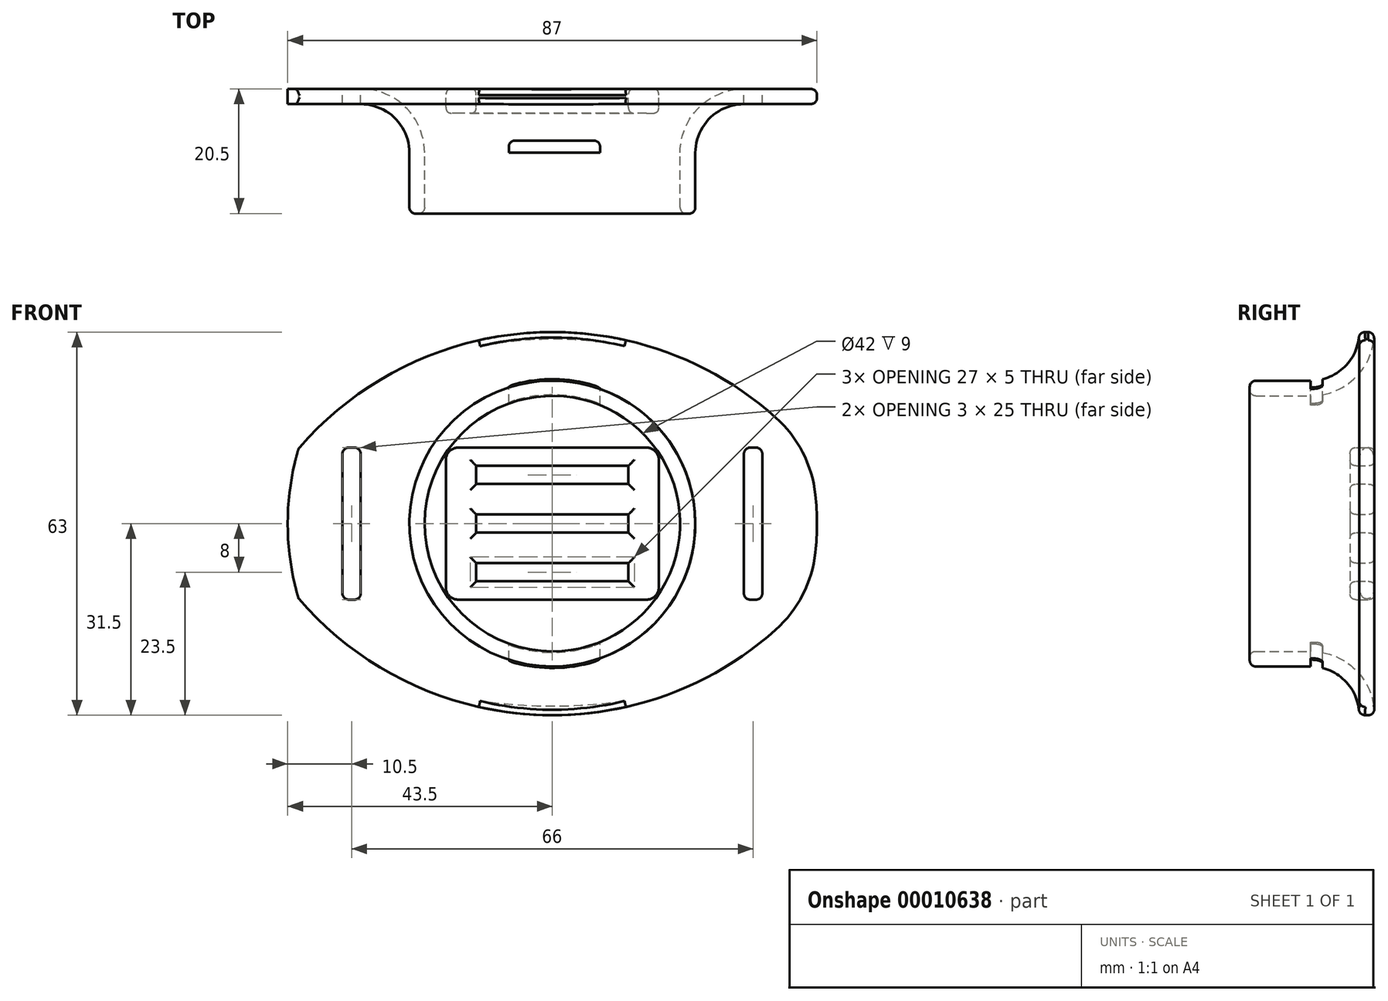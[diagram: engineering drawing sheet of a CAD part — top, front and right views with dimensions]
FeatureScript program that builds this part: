
annotation { "Feature Type Name" : "Feature", "Feature Type Description" : "" }
export const myFeature = defineFeature(function(context is Context, id is Id, definition is map)
    precondition{}
    {
        {
            var Q0;
            Q0=qCreatedBy(makeId("Front.planeOp"),FACE);
            var sketch = newSketch(context, id + "F0", { "sketchPlane" : qUnion([Q0])});
            skEllipse(sketch, "E0", {"center": v(0, 0) * mm, "majorRadius": 23.5 * mm, "minorRadius": 23.5 * mm, "majorAxis": v(1, 0)});
            skLineSegment(sketch, "E1", {"start": v(-23.5, 0) * mm, "end": v(23.5, 0) * mm, "construction": true});
            skLineSegment(sketch, "E2", {"start": v(0, -23.5) * mm, "end": v(0, 23.5) * mm, "construction": true});
            skCircle(sketch, "E3", {"center": v(0, 0) * mm, "radius": 21 * mm});
            skSolve(sketch);
        }
        {
            var Q0;
            Q0=makeQuery(id+"F0.imprint","IMPRINT",FACE,{"disambiguationData":[TD([[makeQuery(id+"F0.imprint","IMPRINT",EDGE,{"derivedFrom":sQuery(id+"F0.wireOp",EDGE,"E0")}),1.0]])]});
            extrude(context, id + "F1", {"entities" : qUnion([Q0]), "depth" : 10 * mm});
        }
        {
            var Q0;
            Q0=qCreatedBy(makeId("Top.planeOp"),FACE);
            var sketch = newSketch(context, id + "F2", { "sketchPlane" : qUnion([Q0])});
            skLineSegment(sketch, "E4.0", {"start": v(23.5, -10) * mm, "end": v(-23.5, -10) * mm, "construction": true});
            skLineSegment(sketch, "E5.0", {"start": v(23.5, 0) * mm, "end": v(-23.5, 0) * mm, "construction": true});
            skLineSegment(sketch, "E6", {"start": v(-23.5, -10) * mm, "end": v(-23.5, 0) * mm, "construction": true});
            skArc(sketch, "E7", {"start": v(31.5, 8) * mm, "mid": v(25.84, 5.66) * mm, "end": v(23.5, 0) * mm});
            skLineSegment(sketch, "E8", {"start": v(31.5, 8) * mm, "end": v(31.5, 10.5) * mm});
            skArc(sketch, "E9", {"start": v(31.5, 10.5) * mm, "mid": v(24.08, 7.42) * mm, "end": v(21, 0) * mm});
            skLineSegment(sketch, "E10", {"start": v(21, 0) * mm, "end": v(23.5, 0) * mm});
            skLineSegment(sketch, "E11", {"start": v(23.5, 0) * mm, "end": v(23.5, -10) * mm, "construction": true});
            skLineSegment(sketch, "E12", {"start": v(23.5, 0) * mm, "end": v(44.37, 0) * mm, "construction": true});
            skLineSegment(sketch, "E13", {"start": v(31.5, 8) * mm, "end": v(43.5, 8) * mm});
            skLineSegment(sketch, "E14", {"start": v(43.5, 8) * mm, "end": v(43.5, 10.5) * mm});
            skLineSegment(sketch, "E15", {"start": v(43.5, 10.5) * mm, "end": v(31.5, 10.5) * mm});
            skSolve(sketch);
        }
        {
            var Q0;
            Q0=qCreatedBy(makeId("Top.planeOp"),FACE);
            var sketch = newSketch(context, id + "F3", { "sketchPlane" : qUnion([Q0])});
            skLineSegment(sketch, "E16.0", {"start": v(23.5, 0) * mm, "end": v(-23.5, 0) * mm, "construction": true});
            skLineSegment(sketch, "E17.0", {"start": v(23.5, -10) * mm, "end": v(-23.5, -10) * mm, "construction": true});
            skLineSegment(sketch, "E18", {"start": v(0, 0) * mm, "end": v(0, -10) * mm, "construction": true});
            skSolve(sketch);
        }
        {
            var Q0;
            Q0 = qSketchRegion(id + "F2", true);
            var Q1;
            Q1=sQuery(id+"F3.wireOp",EDGE,"E18");
            revolve(context, id + "F4", {"operationType" : NewBodyOperationType.ADD, "entities" : qUnion([Q0]), "axis" : qUnion([Q1]), "revolveType" : RevolveType.FULL});
        }
        {
            var Q0;
            Q0=makeQuery(id+"F4.opRevolve","SWEPT_FACE",FACE,{"disambiguationData":[OSD([sQuery(id+"F2.wireOp",EDGE,"E15")])]});
            var sketch = newSketch(context, id + "F5", { "sketchPlane" : qUnion([Q0])});
            skLineSegment(sketch, "E19.bottom", {"start": v(-34.5, 10) * mm, "end": v(-31.5, 10) * mm});
            skLineSegment(sketch, "E19.top", {"start": v(-34.5, -10) * mm, "end": v(-31.5, -10) * mm});
            skLineSegment(sketch, "E19.left", {"start": v(-34.5, 10) * mm, "end": v(-34.5, -10) * mm});
            skLineSegment(sketch, "E19.right", {"start": v(-31.5, 10) * mm, "end": v(-31.5, -10) * mm});
            skCircle(sketch, "E20.0", {"center": v(0, 0) * mm, "radius": 31.5 * mm, "construction": true});
            skLineSegment(sketch, "E21", {"start": v(-31.5, 0) * mm, "end": v(0, 0) * mm, "construction": true});
            skSolve(sketch);
        }
        {
            var Q0;
            {var subQ3=sQuery(id+"F5.wireOp",EDGE,"E19.bottom");Q0=makeQuery(id+"F5.imprint","IMPRINT",FACE,{"disambiguationData":[TD([[makeQuery(id+"F5.imprint","IMPRINT",EDGE,{"derivedFrom":subQ3}),-1.0]])]});}
            extrude(context, id + "F6", {"entities" : qUnion([Q0]), "endBound" : BoundingType.SYMMETRIC, "oppositeDirection" : true, "depth" : 6.64 * mm});
        }
        {
            var Q0;
            Q0=makeQuery(id+"F6.opExtrude","SWEPT_FACE",FACE,{"disambiguationData":[OSD([sQuery(id+"F5.wireOp",EDGE,"E19.left")])]});
            cPlane(context, id + "F7", {"entities" : qUnion([Q0]), "cplaneType" : CPlaneType.OFFSET, "offset" : 1.5 * mm, "width" : 150 * mm, "height" : 150 * mm});
        }
        {
            var Q0;
            Q0=makeQuery(id+"FB1noEDOaeAqazW_2.opPattern","COPY",BODY,{"derivedFrom":makeQuery(id+"F6.opExtrude","SWEPT_BODY",BODY,{"disambiguationData":[OSD([sQuery(id+"F5.wireOp",EDGE,"E19.bottom"),sQuery(id+"F5.wireOp",EDGE,"E19.top"),sQuery(id+"F5.wireOp",EDGE,"E19.left"),sQuery(id+"F5.wireOp",EDGE,"E19.right")])]}),"instanceName":"1"});
            var Q1;
            Q1=makeQuery(id+"F6.opExtrude","SWEPT_BODY",BODY,{"disambiguationData":[OSD([sQuery(id+"F5.wireOp",EDGE,"E19.bottom"),sQuery(id+"F5.wireOp",EDGE,"E19.top"),sQuery(id+"F5.wireOp",EDGE,"E19.left"),sQuery(id+"F5.wireOp",EDGE,"E19.right")])]});
            var Q2;
            Q2=qCreatedBy(makeId("Right.planeOp"),FACE);
            mirror(context, id + "F8", {"entities" : qUnion([Q0, Q1]), "mirrorPlane" : qUnion([Q2])});
        }
        {
            var Q0;
            Q0=makeQuery(id+"F8.opPattern","COPY",BODY,{"derivedFrom":makeQuery(id+"FB1noEDOaeAqazW_2.opPattern","COPY",BODY,{"derivedFrom":makeQuery(id+"F6.opExtrude","SWEPT_BODY",BODY,{"disambiguationData":[OSD([sQuery(id+"F5.wireOp",EDGE,"E19.bottom"),sQuery(id+"F5.wireOp",EDGE,"E19.top"),sQuery(id+"F5.wireOp",EDGE,"E19.left"),sQuery(id+"F5.wireOp",EDGE,"E19.right")])]}),"instanceName":"1"}),"instanceName":"1"});
            var Q1;
            Q1=makeQuery(id+"F8.opPattern","COPY",BODY,{"derivedFrom":makeQuery(id+"F6.opExtrude","SWEPT_BODY",BODY,{"disambiguationData":[OSD([sQuery(id+"F5.wireOp",EDGE,"E19.bottom"),sQuery(id+"F5.wireOp",EDGE,"E19.top"),sQuery(id+"F5.wireOp",EDGE,"E19.left"),sQuery(id+"F5.wireOp",EDGE,"E19.right")])]}),"instanceName":"1"});
            var Q2;
            Q2=makeQuery(id+"F6.opExtrude","SWEPT_BODY",BODY,{"disambiguationData":[OSD([sQuery(id+"F5.wireOp",EDGE,"E19.bottom"),sQuery(id+"F5.wireOp",EDGE,"E19.top"),sQuery(id+"F5.wireOp",EDGE,"E19.left"),sQuery(id+"F5.wireOp",EDGE,"E19.right")])]});
            var Q3;
            Q3=makeQuery(id+"FB1noEDOaeAqazW_2.opPattern","COPY",BODY,{"derivedFrom":makeQuery(id+"F6.opExtrude","SWEPT_BODY",BODY,{"disambiguationData":[OSD([sQuery(id+"F5.wireOp",EDGE,"E19.bottom"),sQuery(id+"F5.wireOp",EDGE,"E19.top"),sQuery(id+"F5.wireOp",EDGE,"E19.left"),sQuery(id+"F5.wireOp",EDGE,"E19.right")])]}),"instanceName":"1"});
            var Q4;
            Q4=makeQuery(id+"F1.opExtrude","SWEPT_BODY",BODY,{"disambiguationData":[OSD([sQuery(id+"F0.wireOp",EDGE,"E0"),sQuery(id+"F0.wireOp",EDGE,"E3")])]});
            booleanBodies(context, id + "F9", {"operationType" : BooleanOperationType.SUBTRACTION, "tools" : qUnion([Q0, Q1, Q2, Q3]), "targets" : qUnion([Q4])});
        }
        {
            var Q0;
            {var subQ5=sQuery(id+"F5.wireOp",EDGE,"E19.bottom");Q0=makeQuery(id+"F5.imprint","IMPRINT",FACE,{"disambiguationData":[TD([[makeQuery(id+"F5.imprint","IMPRINT",EDGE,{"derivedFrom":subQ5}),1.0]])]});}
            var sketch = newSketch(context, id + "F10", { "sketchPlane" : qUnion([Q0])});
            skArc(sketch, "E22.0", {"start": v(31.5, 0) * mm, "mid": v(0, 31.5) * mm, "end": v(-31.5, 0) * mm, "construction": true});
            skLineSegment(sketch, "E23", {"start": v(0, 0) * mm, "end": v(0, 31.5) * mm, "construction": true});
            skArc(sketch, "E24.0", {"start": v(41.7, 12.35) * mm, "mid": v(0, 43.5) * mm, "end": v(-41.7, 12.35) * mm});
            skArc(sketch, "E25", {"start": v(41.7, 12.35) * mm, "mid": v(0, 31.5) * mm, "end": v(-41.7, 12.35) * mm});
            skLineSegment(sketch, "E26", {"start": v(-41.7, 12.35) * mm, "end": v(41.7, 12.35) * mm, "construction": true});
            skArc(sketch, "E27.0", {"start": v(-41.7, -12.35) * mm, "mid": v(0, -43.5) * mm, "end": v(41.7, -12.35) * mm});
            skLineSegment(sketch, "E28", {"start": v(-41.7, -12.35) * mm, "end": v(41.7, -12.35) * mm, "construction": true});
            skArc(sketch, "E29", {"start": v(-41.7, -12.35) * mm, "mid": v(0, -31.5) * mm, "end": v(41.7, -12.35) * mm});
            skCircle(sketch, "E30.0", {"center": v(0, 0) * mm, "radius": 31.5 * mm, "construction": true});
            skSolve(sketch);
        }
        {
            var Q0;
            Q0 = qSketchRegion(id + "F10", true);
            extrude(context, id + "F11", {"entities" : qUnion([Q0]), "operationType" : NewBodyOperationType.REMOVE, "endBound" : BoundingType.UP_TO_NEXT, "oppositeDirection" : true, "depth" : 25 * mm});
        }
        {
            var Q0;
            {var subQ0=sQuery(id+"F2.wireOp",EDGE,"E14");var subQ1=sQuery(id+"F2.wireOp",EDGE,"E15");var subQ2=sQuery(id+"F10.wireOp",EDGE,"E25");var subQ3=sQuery(id+"F10.wireOp",EDGE,"E24.0");Q0=makeQuery(id+"F11.boolean.opBoolean","COPY",EDGE,{"derivedFrom":makeQuery(id+"F11.opExtrude","SWEPT_EDGE",EDGE,{"disambiguationData":[OSD([subQ0,subQ1,subQ2,subQ3]),TDD([makeQuery(id+"F10.imprint","INTERSECT",VERTEX,{"disambiguationData":[OD(1.0)],"derivedFrom":[makeQuery(id+"F5.imprint","IMPRINT",EDGE,{"derivedFrom":makeQuery(id+"F4.opRevolve","SWEPT_EDGE",EDGE,{"disambiguationData":[OSD([subQ0,subQ1])]})}),subQ2,subQ3]})])]})});}
            var Q1;
            {var subQ0=sQuery(id+"F2.wireOp",EDGE,"E14");var subQ1=sQuery(id+"F2.wireOp",EDGE,"E15");var subQ2=sQuery(id+"F10.wireOp",EDGE,"E27.0");var subQ3=sQuery(id+"F10.wireOp",EDGE,"E29");Q1=makeQuery(id+"F11.boolean.opBoolean","COPY",EDGE,{"derivedFrom":makeQuery(id+"F11.opExtrude","SWEPT_EDGE",EDGE,{"disambiguationData":[OSD([subQ0,subQ1,subQ2,subQ3]),TDD([makeQuery(id+"F10.imprint","INTERSECT",VERTEX,{"disambiguationData":[OD(0.0)],"derivedFrom":[makeQuery(id+"F5.imprint","IMPRINT",EDGE,{"derivedFrom":makeQuery(id+"F4.opRevolve","SWEPT_EDGE",EDGE,{"disambiguationData":[OSD([subQ0,subQ1])]})}),subQ2,subQ3]})])]})});}
            var Q2;
            {var subQ0=sQuery(id+"F2.wireOp",EDGE,"E14");var subQ1=sQuery(id+"F2.wireOp",EDGE,"E15");var subQ2=sQuery(id+"F10.wireOp",EDGE,"E27.0");var subQ3=sQuery(id+"F10.wireOp",EDGE,"E29");Q2=makeQuery(id+"F11.boolean.opBoolean","COPY",EDGE,{"derivedFrom":makeQuery(id+"F11.opExtrude","SWEPT_EDGE",EDGE,{"disambiguationData":[OSD([subQ0,subQ1,subQ2,subQ3]),TDD([makeQuery(id+"F10.imprint","INTERSECT",VERTEX,{"disambiguationData":[OD(1.0)],"derivedFrom":[makeQuery(id+"F5.imprint","IMPRINT",EDGE,{"derivedFrom":makeQuery(id+"F4.opRevolve","SWEPT_EDGE",EDGE,{"disambiguationData":[OSD([subQ0,subQ1])]})}),subQ2,subQ3]})])]})});}
            var Q3;
            {var subQ0=sQuery(id+"F2.wireOp",EDGE,"E14");var subQ1=sQuery(id+"F2.wireOp",EDGE,"E15");var subQ2=sQuery(id+"F10.wireOp",EDGE,"E25");var subQ3=sQuery(id+"F10.wireOp",EDGE,"E24.0");Q3=makeQuery(id+"F11.boolean.opBoolean","COPY",EDGE,{"derivedFrom":makeQuery(id+"F11.opExtrude","SWEPT_EDGE",EDGE,{"disambiguationData":[OSD([subQ0,subQ1,subQ2,subQ3]),TDD([makeQuery(id+"F10.imprint","INTERSECT",VERTEX,{"disambiguationData":[OD(0.0)],"derivedFrom":[makeQuery(id+"F5.imprint","IMPRINT",EDGE,{"derivedFrom":makeQuery(id+"F4.opRevolve","SWEPT_EDGE",EDGE,{"disambiguationData":[OSD([subQ0,subQ1])]})}),subQ2,subQ3]})])]})});}
            fillet(context, id + "F12", {"entities" : qUnion([Q0, Q1, Q2, Q3]), "radius" : 20 * mm, "tangentPropagation" : true, "allowEdgeOverflow" : false});
        }
        {
            var Q0;
            {var subQ0=makeQuery(id+"F4.opRevolve","SWEPT_FACE",FACE,{"disambiguationData":[OSD([sQuery(id+"F2.wireOp",EDGE,"E15")])]});var subQ4=makeQuery(id+"F6.opExtrude","SWEPT_FACE",FACE,{"disambiguationData":[OSD([sQuery(id+"F5.wireOp",EDGE,"E19.bottom")])]});Q0=makeQuery(id+"F11.boolean.opBoolean","SPLIT",FACE,{"disambiguationData":[TD([makeQuery(id+"F9.opBoolean","COPY",FACE,{"derivedFrom":subQ4})])],"derivedFrom":subQ0});}
            var sketch = newSketch(context, id + "F13", { "sketchPlane" : qUnion([Q0])});
            skLineSegment(sketch, "E31.bottom", {"start": v(-34.5, 12.5) * mm, "end": v(-31.5, 12.5) * mm});
            skLineSegment(sketch, "E31.top", {"start": v(-34.5, -12.5) * mm, "end": v(-31.5, -12.5) * mm});
            skLineSegment(sketch, "E31.left", {"start": v(-34.5, 12.5) * mm, "end": v(-34.5, -12.5) * mm});
            skLineSegment(sketch, "E31.right", {"start": v(-31.5, 12.5) * mm, "end": v(-31.5, -12.5) * mm});
            skCircle(sketch, "E32.0", {"center": v(0, 0) * mm, "radius": 21 * mm, "construction": true});
            skLineSegment(sketch, "E33", {"start": v(0, 0) * mm, "end": v(-31.5, 0) * mm, "construction": true});
            skLineSegment(sketch, "E34", {"start": v(0, 16.83) * mm, "end": v(0, -14.27) * mm, "construction": true});
            skLineSegment(sketch, "E35.0.MirrorCS", {"start": v(34.5, 12.5) * mm, "end": v(31.5, 12.5) * mm});
            skLineSegment(sketch, "E35.1.MirrorCS", {"start": v(31.5, 12.5) * mm, "end": v(31.5, -12.5) * mm});
            skLineSegment(sketch, "E35.2.MirrorCS", {"start": v(34.5, -12.5) * mm, "end": v(31.5, -12.5) * mm});
            skLineSegment(sketch, "E36.0.MirrorCS", {"start": v(34.5, 12.5) * mm, "end": v(34.5, -12.5) * mm});
            skSolve(sketch);
        }
        {
            var Q0;
            Q0 = qSketchRegion(id + "F13", true);
            extrude(context, id + "F14", {"entities" : qUnion([Q0]), "operationType" : NewBodyOperationType.REMOVE, "endBound" : BoundingType.THROUGH_ALL, "oppositeDirection" : true, "depth" : 25 * mm});
        }
        {
            var Q0;
            Q0=makeQuery(id+"F11.boolean.opBoolean","COPY",FACE,{"derivedFrom":makeQuery(id+"F11.opExtrude","SWEPT_FACE",FACE,{"disambiguationData":[OSD([sQuery(id+"F10.wireOp",EDGE,"E25")])]})});
            var Q1;
            Q1=makeQuery(id+"F1.opExtrude","CAP_FACE",FACE,{"disambiguationData":[OSD([sQuery(id+"F0.wireOp",EDGE,"E0"),sQuery(id+"F0.wireOp",EDGE,"E3")])],"isStart":false});
            fillet(context, id + "F15", {"entities" : qUnion([Q0, Q1]), "radius" : 1 * mm, "tangentPropagation" : true, "allowEdgeOverflow" : false});
        }
        {
            var Q0;
            Q0=qCreatedBy(makeId("Top.planeOp"),FACE);
            var sketch = newSketch(context, id + "F16", { "sketchPlane" : qUnion([Q0])});
            skLineSegment(sketch, "E37.bottom", {"start": v(-7.16, 2) * mm, "end": v(7.84, 2) * mm});
            skLineSegment(sketch, "E37.top", {"start": v(-7.16, 0) * mm, "end": v(7.84, 0) * mm});
            skLineSegment(sketch, "E37.left", {"start": v(-7.16, 2) * mm, "end": v(-7.16, 0) * mm});
            skLineSegment(sketch, "E37.right", {"start": v(7.84, 2) * mm, "end": v(7.84, 0) * mm});
            skLineSegment(sketch, "E38.0", {"start": v(-23.5, 0) * mm, "end": v(23.5, 0) * mm});
            skSolve(sketch);
        }
        {
            var Q0;
            Q0 = qSketchRegion(id + "F16", true);
            extrude(context, id + "F17", {"entities" : qUnion([Q0]), "operationType" : NewBodyOperationType.REMOVE, "oppositeDirection" : true, "depth" : 25 * mm, "hasSecondDirection" : true, "secondDirectionOppositeDirection" : false, "secondDirectionDepth" : 25 * mm});
        }
        {
            var Q0;
            Q0=makeQuery(id+"F17.boolean.opBoolean","COPY",EDGE,{"disambiguationData":[OD(1.0)],"derivedFrom":makeQuery(id+"F17.opExtrude","SWEPT_EDGE",EDGE,{"disambiguationData":[OSD([sQuery(id+"F16.wireOp",EDGE,"E37.right"),sQuery(id+"F16.wireOp",EDGE,"E38.0")])]})});
            var Q1;
            Q1=makeQuery(id+"F17.boolean.opBoolean","COPY",EDGE,{"disambiguationData":[OD(1.0)],"derivedFrom":makeQuery(id+"F17.opExtrude","SWEPT_EDGE",EDGE,{"disambiguationData":[OSD([sQuery(id+"F16.wireOp",EDGE,"E37.bottom"),sQuery(id+"F16.wireOp",EDGE,"E37.right")])]})});
            var Q2;
            Q2=makeQuery(id+"F17.boolean.opBoolean","COPY",EDGE,{"disambiguationData":[OD(1.0)],"derivedFrom":makeQuery(id+"F17.opExtrude","SWEPT_EDGE",EDGE,{"disambiguationData":[OSD([sQuery(id+"F16.wireOp",EDGE,"E37.bottom"),sQuery(id+"F16.wireOp",EDGE,"E37.left")])]})});
            var Q3;
            Q3=makeQuery(id+"F17.boolean.opBoolean","COPY",EDGE,{"disambiguationData":[OD(1.0)],"derivedFrom":makeQuery(id+"F17.opExtrude","SWEPT_EDGE",EDGE,{"disambiguationData":[OSD([sQuery(id+"F16.wireOp",EDGE,"E37.left"),sQuery(id+"F16.wireOp",EDGE,"E38.0")])]})});
            var Q4;
            Q4=makeQuery(id+"F17.boolean.opBoolean","COPY",EDGE,{"disambiguationData":[OD(0.0)],"derivedFrom":makeQuery(id+"F17.opExtrude","SWEPT_EDGE",EDGE,{"disambiguationData":[OSD([sQuery(id+"F16.wireOp",EDGE,"E37.bottom"),sQuery(id+"F16.wireOp",EDGE,"E37.left")])]})});
            var Q5;
            Q5=makeQuery(id+"F17.boolean.opBoolean","COPY",EDGE,{"disambiguationData":[OD(0.0)],"derivedFrom":makeQuery(id+"F17.opExtrude","SWEPT_EDGE",EDGE,{"disambiguationData":[OSD([sQuery(id+"F16.wireOp",EDGE,"E37.bottom"),sQuery(id+"F16.wireOp",EDGE,"E37.right")])]})});
            var Q6;
            Q6=makeQuery(id+"F17.boolean.opBoolean","COPY",EDGE,{"disambiguationData":[OD(0.0)],"derivedFrom":makeQuery(id+"F17.opExtrude","SWEPT_EDGE",EDGE,{"disambiguationData":[OSD([sQuery(id+"F16.wireOp",EDGE,"E37.right"),sQuery(id+"F16.wireOp",EDGE,"E38.0")])]})});
            var Q7;
            Q7=makeQuery(id+"F17.boolean.opBoolean","COPY",EDGE,{"disambiguationData":[OD(0.0)],"derivedFrom":makeQuery(id+"F17.opExtrude","SWEPT_EDGE",EDGE,{"disambiguationData":[OSD([sQuery(id+"F16.wireOp",EDGE,"E37.left"),sQuery(id+"F16.wireOp",EDGE,"E38.0")])]})});
            var Q8;
            Q8=makeQuery(id+"F14.boolean.opBoolean","COPY",EDGE,{"derivedFrom":makeQuery(id+"F14.opExtrude","SWEPT_EDGE",EDGE,{"disambiguationData":[OSD([sQuery(id+"F13.wireOp",EDGE,"E35.0.MirrorCS"),sQuery(id+"F13.wireOp",EDGE,"E36.0.MirrorCS")])]})});
            var Q9;
            Q9=makeQuery(id+"F14.boolean.opBoolean","COPY",EDGE,{"derivedFrom":makeQuery(id+"F14.opExtrude","SWEPT_EDGE",EDGE,{"disambiguationData":[OSD([sQuery(id+"F13.wireOp",EDGE,"E35.0.MirrorCS"),sQuery(id+"F13.wireOp",EDGE,"E35.1.MirrorCS")])]})});
            var Q10;
            Q10=makeQuery(id+"F14.boolean.opBoolean","COPY",EDGE,{"derivedFrom":makeQuery(id+"F14.opExtrude","SWEPT_EDGE",EDGE,{"disambiguationData":[OSD([sQuery(id+"F13.wireOp",EDGE,"E35.1.MirrorCS"),sQuery(id+"F13.wireOp",EDGE,"E35.2.MirrorCS")])]})});
            var Q11;
            Q11=makeQuery(id+"F14.boolean.opBoolean","COPY",EDGE,{"derivedFrom":makeQuery(id+"F14.opExtrude","SWEPT_EDGE",EDGE,{"disambiguationData":[OSD([sQuery(id+"F13.wireOp",EDGE,"E35.2.MirrorCS"),sQuery(id+"F13.wireOp",EDGE,"E36.0.MirrorCS")])]})});
            var Q12;
            Q12=makeQuery(id+"F14.boolean.opBoolean","COPY",EDGE,{"derivedFrom":makeQuery(id+"F14.opExtrude","SWEPT_EDGE",EDGE,{"disambiguationData":[OSD([sQuery(id+"F13.wireOp",EDGE,"E31.top"),sQuery(id+"F13.wireOp",EDGE,"E31.right")])]})});
            var Q13;
            Q13=makeQuery(id+"F14.boolean.opBoolean","COPY",EDGE,{"derivedFrom":makeQuery(id+"F14.opExtrude","SWEPT_EDGE",EDGE,{"disambiguationData":[OSD([sQuery(id+"F13.wireOp",EDGE,"E31.bottom"),sQuery(id+"F13.wireOp",EDGE,"E31.right")])]})});
            var Q14;
            Q14=makeQuery(id+"F14.boolean.opBoolean","COPY",EDGE,{"derivedFrom":makeQuery(id+"F14.opExtrude","SWEPT_EDGE",EDGE,{"disambiguationData":[OSD([sQuery(id+"F13.wireOp",EDGE,"E31.bottom"),sQuery(id+"F13.wireOp",EDGE,"E31.left")])]})});
            var Q15;
            Q15=makeQuery(id+"F14.boolean.opBoolean","COPY",EDGE,{"derivedFrom":makeQuery(id+"F14.opExtrude","SWEPT_EDGE",EDGE,{"disambiguationData":[OSD([sQuery(id+"F13.wireOp",EDGE,"E31.top"),sQuery(id+"F13.wireOp",EDGE,"E31.left")])]})});
            fillet(context, id + "F18", {"entities" : qUnion([Q0, Q1, Q2, Q3, Q4, Q5, Q6, Q7, Q8, Q9, Q10, Q11, Q12, Q13, Q14, Q15]), "radius" : 1 * mm, "tangentPropagation" : true, "allowEdgeOverflow" : false});
        }
        {
            var Q0;
            {var subQ0=makeQuery(id+"F4.opRevolve","SWEPT_FACE",FACE,{"disambiguationData":[OSD([sQuery(id+"F2.wireOp",EDGE,"E15")])]});Q0=makeQuery(id+"F11.boolean.opBoolean","SPLIT",FACE,{"disambiguationData":[TD([makeQuery(id+"F9.opBoolean","COPY",FACE,{"derivedFrom":makeQuery(id+"F8.opPattern","COPY",FACE,{"derivedFrom":makeQuery(id+"F6.opExtrude","SWEPT_FACE",FACE,{"disambiguationData":[OSD([sQuery(id+"F5.wireOp",EDGE,"E19.bottom")])]}),"instanceName":"1"})})])],"derivedFrom":subQ0});}
            var sketch = newSketch(context, id + "F19", { "sketchPlane" : qUnion([Q0])});
            skLineSegment(sketch, "E39.bottom", {"start": v(-15.5, 12.5) * mm, "end": v(15.5, 12.5) * mm});
            skLineSegment(sketch, "E39.top", {"start": v(-15.5, -12.5) * mm, "end": v(15.5, -12.5) * mm});
            skLineSegment(sketch, "E39.left", {"start": v(-17.5, 10.5) * mm, "end": v(-17.5, -10.5) * mm});
            skLineSegment(sketch, "E39.right", {"start": v(17.5, 10.5) * mm, "end": v(17.5, -10.5) * mm});
            skPoint(sketch, "E40.visualSharp", {"position": v(-17.5, 12.5) * mm});
            skArc(sketch, "E40.filletArc", {"start": v(-15.5, 12.5) * mm, "mid": v(-16.91, 11.91) * mm, "end": v(-17.5, 10.5) * mm});
            skPoint(sketch, "E41.visualSharp", {"position": v(-17.5, -12.5) * mm});
            skArc(sketch, "E41.filletArc", {"start": v(-17.5, -10.5) * mm, "mid": v(-16.91, -11.91) * mm, "end": v(-15.5, -12.5) * mm});
            skPoint(sketch, "E42.visualSharp", {"position": v(17.5, -12.5) * mm});
            skArc(sketch, "E42.filletArc", {"start": v(15.5, -12.5) * mm, "mid": v(16.91, -11.91) * mm, "end": v(17.5, -10.5) * mm});
            skPoint(sketch, "E43.visualSharp", {"position": v(17.5, 12.5) * mm});
            skArc(sketch, "E43.filletArc", {"start": v(17.5, 10.5) * mm, "mid": v(16.91, 11.91) * mm, "end": v(15.5, 12.5) * mm});
            skLineSegment(sketch, "E44.rect.bottom", {"start": v(12.5, 6.5) * mm, "end": v(-12.5, 6.5) * mm});
            skLineSegment(sketch, "E44.rect.top", {"start": v(12.5, 9.5) * mm, "end": v(-12.5, 9.5) * mm});
            skLineSegment(sketch, "E44.rect.left", {"start": v(12.5, 6.5) * mm, "end": v(12.5, 9.5) * mm});
            skLineSegment(sketch, "E44.rect.right", {"start": v(-12.5, 6.5) * mm, "end": v(-12.5, 9.5) * mm});
            skPoint(sketch, "E44.rect.middle", {"position": v(0, 8) * mm});
            skLineSegment(sketch, "E45.rect.bottom", {"start": v(12.5, 1.5) * mm, "end": v(-12.5, 1.5) * mm});
            skLineSegment(sketch, "E45.rect.top", {"start": v(12.5, -1.5) * mm, "end": v(-12.5, -1.5) * mm});
            skLineSegment(sketch, "E45.rect.left", {"start": v(12.5, 1.5) * mm, "end": v(12.5, -1.5) * mm});
            skLineSegment(sketch, "E45.rect.right", {"start": v(-12.5, 1.5) * mm, "end": v(-12.5, -1.5) * mm});
            skLineSegment(sketch, "E46.rect.bottom", {"start": v(12.5, -6.5) * mm, "end": v(-12.5, -6.5) * mm});
            skLineSegment(sketch, "E46.rect.top", {"start": v(12.5, -9.5) * mm, "end": v(-12.5, -9.5) * mm});
            skLineSegment(sketch, "E46.rect.left", {"start": v(12.5, -6.5) * mm, "end": v(12.5, -9.5) * mm});
            skLineSegment(sketch, "E46.rect.right", {"start": v(-12.5, -6.5) * mm, "end": v(-12.5, -9.5) * mm});
            skPoint(sketch, "E46.rect.middle", {"position": v(0, -8) * mm});
            skLineSegment(sketch, "E47.0", {"start": v(-34.5, -11.5) * mm, "end": v(-34.5, 11.5) * mm, "construction": true});
            skLineSegment(sketch, "E48.0", {"start": v(-33.5, 12.5) * mm, "end": v(-32.5, 12.5) * mm});
            skSolve(sketch);
        }
        {
            var Q0;
            Q0=makeQuery(id+"F19.imprint","IMPRINT",FACE,{"disambiguationData":[TD([[makeQuery(id+"F19.imprint","IMPRINT",EDGE,{"derivedFrom":sQuery(id+"F19.wireOp",EDGE,"E39.bottom")}),-1.0]])]});
            extrude(context, id + "F20", {"entities" : qUnion([Q0]), "oppositeDirection" : true, "depth" : 4 * mm});
        }
        {
            var Q0;
            Q0=makeQuery(id+"F20.opExtrude","CAP_FACE",FACE,{"disambiguationData":[OSD([sQuery(id+"F19.wireOp",EDGE,"E39.bottom"),sQuery(id+"F19.wireOp",EDGE,"E39.top"),sQuery(id+"F19.wireOp",EDGE,"E39.left"),sQuery(id+"F19.wireOp",EDGE,"E39.right"),sQuery(id+"F19.wireOp",EDGE,"E40.filletArc"),sQuery(id+"F19.wireOp",EDGE,"E41.filletArc"),sQuery(id+"F19.wireOp",EDGE,"E42.filletArc"),sQuery(id+"F19.wireOp",EDGE,"E43.filletArc"),sQuery(id+"F19.wireOp",EDGE,"E44.rect.bottom"),sQuery(id+"F19.wireOp",EDGE,"E44.rect.top"),sQuery(id+"F19.wireOp",EDGE,"E44.rect.left"),sQuery(id+"F19.wireOp",EDGE,"E44.rect.right"),sQuery(id+"F19.wireOp",EDGE,"E45.rect.bottom"),sQuery(id+"F19.wireOp",EDGE,"E45.rect.top"),sQuery(id+"F19.wireOp",EDGE,"E45.rect.left"),sQuery(id+"F19.wireOp",EDGE,"E45.rect.right"),sQuery(id+"F19.wireOp",EDGE,"E46.rect.bottom"),sQuery(id+"F19.wireOp",EDGE,"E46.rect.top"),sQuery(id+"F19.wireOp",EDGE,"E46.rect.left"),sQuery(id+"F19.wireOp",EDGE,"E46.rect.right")])],"isStart":true});
            var Q1;
            Q1=makeQuery(id+"F20.opExtrude","CAP_FACE",FACE,{"disambiguationData":[OSD([sQuery(id+"F19.wireOp",EDGE,"E39.bottom"),sQuery(id+"F19.wireOp",EDGE,"E39.top"),sQuery(id+"F19.wireOp",EDGE,"E39.left"),sQuery(id+"F19.wireOp",EDGE,"E39.right"),sQuery(id+"F19.wireOp",EDGE,"E40.filletArc"),sQuery(id+"F19.wireOp",EDGE,"E41.filletArc"),sQuery(id+"F19.wireOp",EDGE,"E42.filletArc"),sQuery(id+"F19.wireOp",EDGE,"E43.filletArc"),sQuery(id+"F19.wireOp",EDGE,"E44.rect.bottom"),sQuery(id+"F19.wireOp",EDGE,"E44.rect.top"),sQuery(id+"F19.wireOp",EDGE,"E44.rect.left"),sQuery(id+"F19.wireOp",EDGE,"E44.rect.right"),sQuery(id+"F19.wireOp",EDGE,"E45.rect.bottom"),sQuery(id+"F19.wireOp",EDGE,"E45.rect.top"),sQuery(id+"F19.wireOp",EDGE,"E45.rect.left"),sQuery(id+"F19.wireOp",EDGE,"E45.rect.right"),sQuery(id+"F19.wireOp",EDGE,"E46.rect.bottom"),sQuery(id+"F19.wireOp",EDGE,"E46.rect.top"),sQuery(id+"F19.wireOp",EDGE,"E46.rect.left"),sQuery(id+"F19.wireOp",EDGE,"E46.rect.right")])],"isStart":false});
            fillet(context, id + "F21", {"entities" : qUnion([Q0, Q1]), "radius" : 1 * mm, "tangentPropagation" : true, "rho" : 0.5, "crossSection" : FilletCrossSection.CONIC, "allowEdgeOverflow" : false});
        }
    });
